# Revit family: IS_iLifeB_T5003_BIM_NL
name_source: partatom
category: Plumbing Fixtures
units: mm (PartAtom-declared; Revit-internal decimal feet)

## family parameters
Always vertical = No
Cut with Voids When Loaded = No
OmniClass Number = 23.45.05.21.11.11
OmniClass Title = Water Operated Water Closets
Part Type = Normal
Room Calculation Point = No
Round Connector Dimension = Use Diameter
Shared = No
Work Plane-Based = No

## types (1)
- T500301 - Ideal Standard i.life B sandwich seat, softclose,  easy-take off push button, adjustable hinge - White Finish
    Accessories = https://www.idealstandard.nl
    Afmetingen = 362 x 449 x 49 mm
    AfstandsEenheid = Millimeter
    Afwerking = Weiß
    AreaUnits = millimetres
    Artikelnummer = T500301
    Artikelomschrijving = Ideal Standard i.life B Sandwichsitz, Softclose, leicht abnehmbarer Druckknopf, verstellbares Scharnier, weiß, im Karton, im Umkarton, EU-Palette
    Artikelreferentie = Ideal Standard i.life B sandwich seat, softclose,  easy-take off push button, adjustable hinge - White Finish
    AssetType = Fixed
    Auteur = Ideal Standard
    BIMObjectName = IS_IdealStandard_WCseatsandcovers_i.lifeB_T5003
    BIMobject category = Toilet Seats
    BIMobject category code = toilet-seats
    BIMobject main category = Sanitary
    BIMobject main category code = sanitary
    BarCode = 8014140501121
    Barcode = 8014140501121
    Beschrijvinggarantie = Herstellergarantie
    BimObjectNaam = IS_IdealStandard_WCseatsandcovers_i.lifeB_T5003
    Brand = Ideal Standard
    Brand url = http://www.idealstandard.nl
    Breedte = 362.000707
    BrutoGewicht = 0
    Category = Sanitary
    Classification = Seats & Covers
    Color = White
    ConnectionType = Plumbing
    Cost = 0 $
    CurrencyUnit = €
    CurrentRevision = 1
    Date of publishing = 22/07/2022
    Description = Ideal Standard i.life B sandwich seat, softclose,  easy-take off push button, adjustable hinge, white, in carton box, in master box, EU pallet
    Diepte = 449 mm
    DurationUnit = Years
    DuurEenheid = Jahre
    Edition number = 1
    Eigenschappen = Sandwichsitz, Softclose, leicht abnehmbarer Druckknopf, verstellbares Scharnier, weiß, im Karton, im Umkarton, EU-Palette
    ElementType = Fixed
    ExpectedLife = 5
    Features = sandwich seat, softclose,  easy-take off push button, adjustable hinge, white, in carton box, in master box, EU pallet
    Finish = White
    GTIN code = https://8014140501121
    GarantieduurInstallatie = https://www.idealstandard.nl
    Garantieonderdelen = https://www.idealstandard.nl
    Garantieunits = Jahre
    GemaaktOp = 22/07/2022
    Help = https://www.idealstandard.nl
    Hoogte = 49.3481018543243
    Hulp = https://www.idealstandard.nl
    IFC Classification = Sanitary Terminal
    IfcExportAs = IfcSanitaryTerminalType
    IfcExportType = WCSEAT
    Installatieinstructies = https://www.idealstandard.nl
    Installation instructions = https://www.idealstandard.nl
    InstallationInstructions = https://www.idealstandard.nl
    Kleur = Weiß
    Lengte = 449 mm
    LinearUnits = millimetres
    MainColor = White
    MaintenanceInformation = https://www.idealstandard.nl
    Manufacturer = Ideal Standard
    Manufacturer name = Ideal Standard
    ManufacturerURL = https://www.idealstandard.nl
    Materiaal = Acryl-
    Material = Fireclay
    Material main = Fireclay
    Merk = Ideal Standard
    Model = T500301
    ModelNumber = T500301
    ModelReference = Ideal Standard i.life B sandwich seat, softclose,  easy-take off push button, adjustable hinge
    NBS Reference Code = 45-35-70/391
    NBS Reference Description = WC seats and covers
    Name = WCseatsandcovers_i.lifeB_T5003_IdealStandard
    NettWeight = 2.08
    Nettogewicht = 2.08
    NominalDepth = 449 mm
    NominalHeight = 49 mm
    NominalLength = 449 mm
    NominalWidth = 362 mm
    Normen = WCseatsandcovers_i.lifeB_T5003_IdealStandard
    OmniClass Code = 23-31 19 00
    OmniClass Description = Toilets
    OppervlakteEenheid = Millimeter
    PredefinedType = Seats & Cover
    Product Guid = 3c34a18b-e72c-4dc1-963c-5f52b295e2b1
    Product SKU = T5003
    Product certification = https://www.idealstandard.nl
    Product data url = https://bimobject.com
    Product family = I.Life B
    Product group = Sanitary
    Product name = I.Life b sandwich seat, softclose
    Product url = https://www.idealstandard.nl
    ProductInformation = https://www.idealstandard.nl
    Productinformatie = https://www.idealstandard.nl
    QR code = http://bimobject.com
    Revisie = 1
    SeatColor = White
    SeatHasCover = No
    SeatMaterial = Acrylic
    SeatType = Soft Close
    Shape = sculptured
    Size = 362 x 449 x 49 mm
    Space = Internal
    SpareParts = https://www.idealstandard.nl
    Technical description = https://www.idealstandard.nl
    Telefoonnummer = 077 355 08 08
    Toepassing = WC Seat & Cover
    Typeconnectie = Installation
    UNSPSC Code = 301815
    URL = https://www.idealstandard.nl
    Uniclass 2015 Code = Pr_40_20_93_95
    Uniclass 2015 Name = WC seats and covers
    Uniclass2015Beschrijving = WC seats and covers
    Uniclass2015Code = Pr_40_20_93_95
    Uniclass2015Referentie = Pr_40_20_93_95
    Uniclass2015Title = WC seats and covers
    Uniclass2015Version = v1.26
    Urlproducent = https://www.idealstandard.nl
    ValutaEenheid = Euro
    Versie = 1
    Version = 1
    Vervangingskosten = 0
    Verwachtelevensduur = 2
    VolumeUnits = Liters
    Volumeunits = Liter
    Vorm = geformt
    WRASURL = https://www.wrasapprovals.co.uk
    WarrantyDescription = manufacturer warranty
    WarrantyDurationUnit = Years
    Weight Net (Kg) = 2.08
    Wisselstukken = https://www.idealstandard.nl
    Youtube clip = https://www.youtube.com

## geometry (parser evidence)
native form markers: Sweep x3
no freeform markers — native parametric forms only
